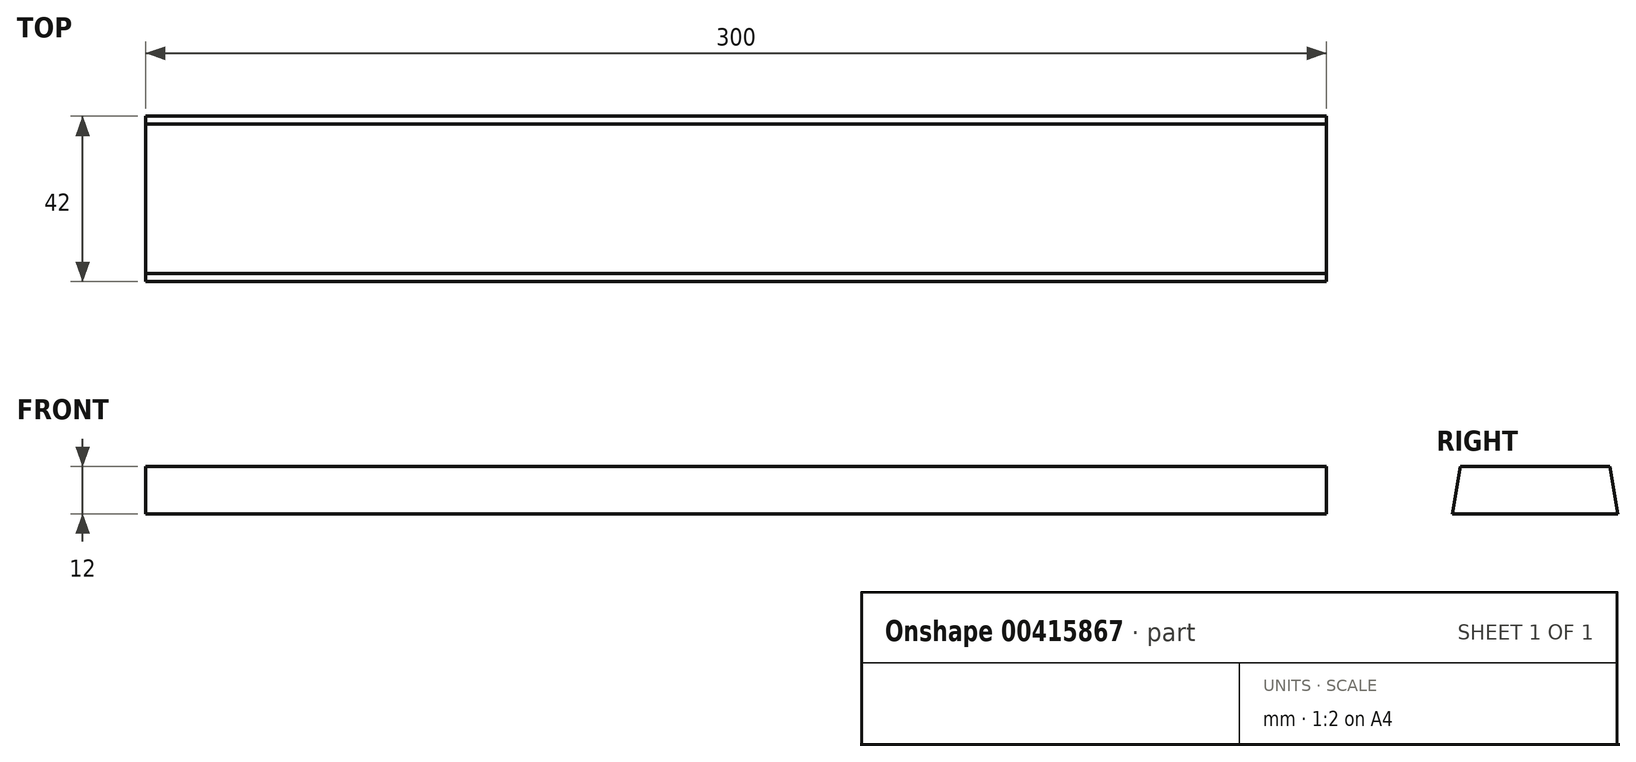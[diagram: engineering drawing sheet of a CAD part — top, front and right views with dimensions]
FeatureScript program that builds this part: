
annotation { "Feature Type Name" : "Feature", "Feature Type Description" : "" }
export const myFeature = defineFeature(function(context is Context, id is Id, definition is map)
    precondition{}
    {
        {
            var Q0;
            Q0=qCreatedBy(makeId("Right.planeOp"),FACE);
            var sketch = newSketch(context, id + "F0", { "sketchPlane" : qUnion([Q0])});
            skLineSegment(sketch, "E0.bottom", {"start": v(-19, 7.33) * mm, "end": v(19, 7.33) * mm});
            skLineSegment(sketch, "E0.top", {"start": v(-19, -4.67) * mm, "end": v(19, -4.67) * mm});
            skLineSegment(sketch, "E0.left", {"start": v(-19, 7.33) * mm, "end": v(-19, -4.67) * mm});
            skLineSegment(sketch, "E0.right", {"start": v(19, 7.33) * mm, "end": v(19, -4.67) * mm});
            skPoint(sketch, "E0.middle", {"position": v(0, 1.33) * mm});
            skLineSegment(sketch, "E1", {"start": v(19, -4.67) * mm, "end": v(21, -4.67) * mm});
            skLineSegment(sketch, "E2", {"start": v(21, -4.67) * mm, "end": v(19, 7.33) * mm});
            skLineSegment(sketch, "E3", {"start": v(-19, 7.33) * mm, "end": v(-21, -4.67) * mm});
            skLineSegment(sketch, "E4", {"start": v(-21, -4.67) * mm, "end": v(-19, -4.67) * mm});
            skSolve(sketch);
        }
        {
            var Q0;
            Q0=makeQuery(id+"F0.imprint","IMPRINT",FACE,{"disambiguationData":[TD([[makeQuery(id+"F0.imprint","IMPRINT",EDGE,{"derivedFrom":sQuery(id+"F0.wireOp",EDGE,"E0.bottom")}),-1.0]])]});
            var Q1;
            Q1=makeQuery(id+"F0.imprint","IMPRINT",FACE,{"disambiguationData":[TD([[makeQuery(id+"F0.imprint","IMPRINT",EDGE,{"derivedFrom":sQuery(id+"F0.wireOp",EDGE,"E0.left")}),-1.0]])]});
            var Q2;
            Q2=makeQuery(id+"F0.imprint","IMPRINT",FACE,{"disambiguationData":[TD([[makeQuery(id+"F0.imprint","IMPRINT",EDGE,{"derivedFrom":sQuery(id+"F0.wireOp",EDGE,"E0.right")}),1.0]])]});
            extrude(context, id + "F1", {"entities" : qUnion([Q0, Q1, Q2]), "depth" : 300 * mm});
        }
    });
